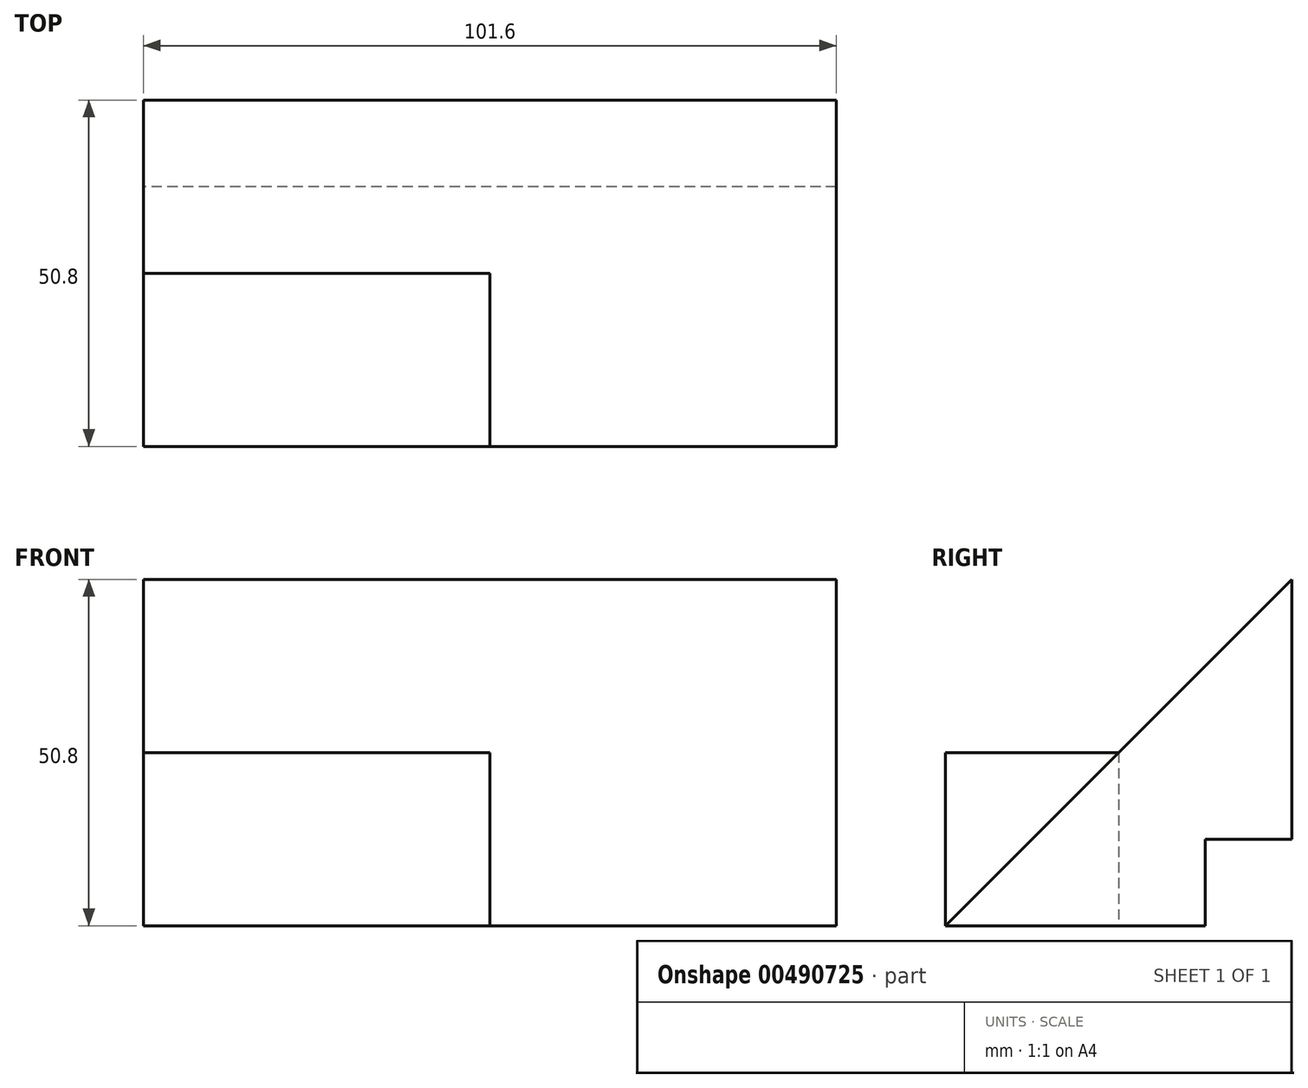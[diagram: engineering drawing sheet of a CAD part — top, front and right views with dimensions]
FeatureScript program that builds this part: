
annotation { "Feature Type Name" : "Feature", "Feature Type Description" : "" }
export const myFeature = defineFeature(function(context is Context, id is Id, definition is map)
    precondition{}
    {
        {
            var Q0;
            Q0=qCreatedBy(makeId("Right.planeOp"),FACE);
            var sketch = newSketch(context, id + "F0", { "sketchPlane" : qUnion([Q0])});
            skLineSegment(sketch, "E0", {"start": v(50.8, 50.8) * mm, "end": v(50.8, 12.7) * mm});
            skLineSegment(sketch, "E1", {"start": v(0, 0) * mm, "end": v(38.1, 0) * mm});
            skLineSegment(sketch, "E2", {"start": v(0, 0) * mm, "end": v(50.8, 50.8) * mm});
            skLineSegment(sketch, "E3", {"start": v(38.1, 0) * mm, "end": v(38.1, 12.7) * mm});
            skLineSegment(sketch, "E4", {"start": v(38.1, 12.7) * mm, "end": v(50.8, 12.7) * mm});
            skSolve(sketch);
        }
        {
            var Q0;
            Q0 = qSketchRegion(id + "F0", true);
            extrude(context, id + "F1", {"entities" : qUnion([Q0]), "depth" : 101.6 * mm});
        }
        {
            var Q0;
            Q0=qCreatedBy(makeId("Top.planeOp"),FACE);
            var sketch = newSketch(context, id + "F2", { "sketchPlane" : qUnion([Q0])});
            skLineSegment(sketch, "E5", {"start": v(0, 0) * mm, "end": v(50.8, 0) * mm});
            skLineSegment(sketch, "E6", {"start": v(50.8, 25.4) * mm, "end": v(0, 25.4) * mm});
            skLineSegment(sketch, "E7", {"start": v(0, 25.4) * mm, "end": v(0, 0) * mm});
            skLineSegment(sketch, "E8", {"start": v(50.8, 25.4) * mm, "end": v(50.8, 0) * mm});
            skSolve(sketch);
        }
        {
            var Q0;
            Q0 = qSketchRegion(id + "F2", true);
            extrude(context, id + "F3", {"entities" : qUnion([Q0]), "depth" : 25.4 * mm});
        }
    });
